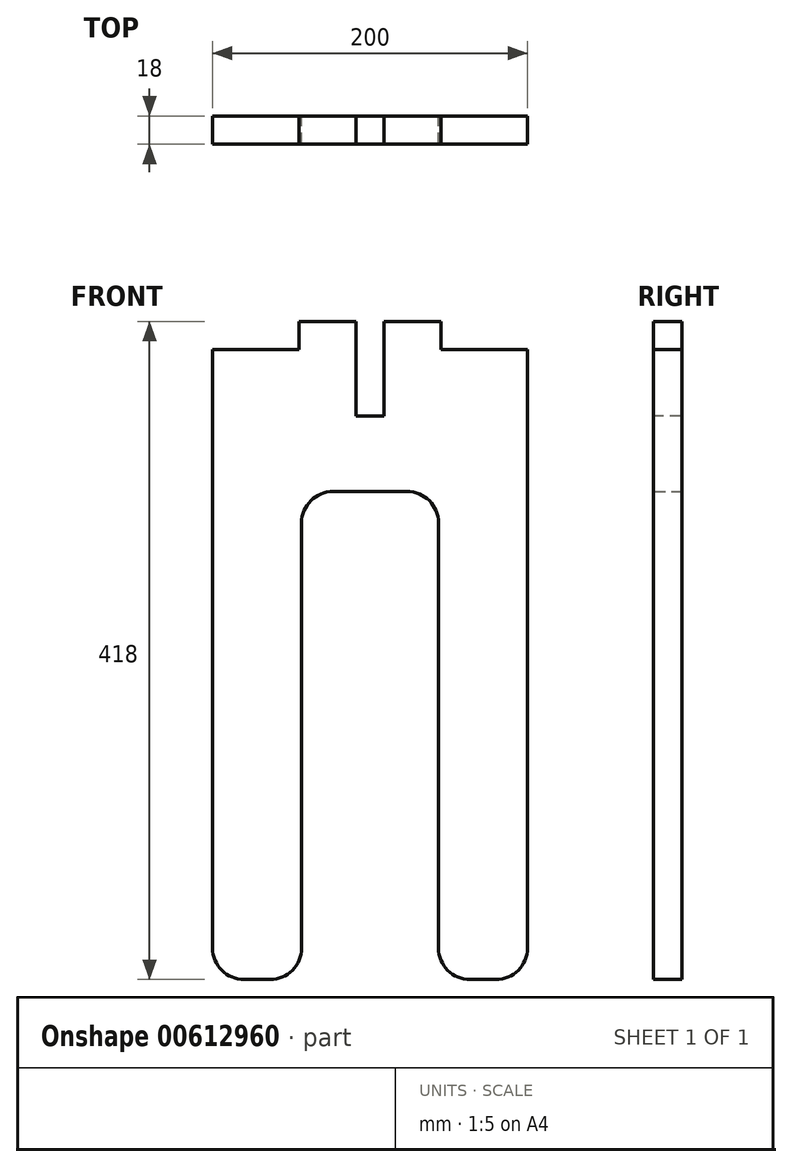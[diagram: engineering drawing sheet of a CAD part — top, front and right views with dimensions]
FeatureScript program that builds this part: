
annotation { "Feature Type Name" : "Feature", "Feature Type Description" : "" }
export const myFeature = defineFeature(function(context is Context, id is Id, definition is map)
    precondition{}
    {
        {
            var Q0;
            Q0=qCreatedBy(makeId("Front.planeOp"),FACE);
            var sketch = newSketch(context, id + "F0", { "sketchPlane" : qUnion([Q0])});
            skLineSegment(sketch, "E0.bottom", {"start": v(78.55, -167.28) * mm, "end": v(62.03, -167.28) * mm});
            skLineSegment(sketch, "E0.top", {"start": v(98.55, 232.72) * mm, "end": v(43.55, 232.72) * mm});
            skLineSegment(sketch, "E0.left", {"start": v(98.55, -147.28) * mm, "end": v(98.55, 232.72) * mm});
            skLineSegment(sketch, "E0.right", {"start": v(-101.45, -147.28) * mm, "end": v(-101.45, 232.72) * mm});
            skPoint(sketch, "E0.middle", {"position": v(-1.45, 32.72) * mm});
            skLineSegment(sketch, "E1.top", {"start": v(22.03, 142.72) * mm, "end": v(-24.93, 142.72) * mm});
            skLineSegment(sketch, "E1.left", {"start": v(42.03, -77.28) * mm, "end": v(42.03, 122.72) * mm});
            skLineSegment(sketch, "E1.right", {"start": v(-44.93, -77.28) * mm, "end": v(-44.93, 122.72) * mm});
            skLineSegment(sketch, "E2", {"start": v(-44.93, -77.28) * mm, "end": v(-44.93, -147.28) * mm});
            skLineSegment(sketch, "E3", {"start": v(42.03, -147.28) * mm, "end": v(42.03, -77.28) * mm});
            skLineSegment(sketch, "E4.trimOffspring", {"start": v(-64.93, -167.28) * mm, "end": v(-81.45, -167.28) * mm});
            skPoint(sketch, "E5.orphan", {"position": v(42.03, -259.35) * mm});
            skPoint(sketch, "E6.visualSharp", {"position": v(-44.93, -167.28) * mm});
            skArc(sketch, "E6.filletArc", {"start": v(-64.93, -167.28) * mm, "mid": v(-50.79, -161.42) * mm, "end": v(-44.93, -147.28) * mm});
            skPoint(sketch, "E7.visualSharp", {"position": v(42.03, -167.28) * mm});
            skArc(sketch, "E7.filletArc", {"start": v(42.03, -147.28) * mm, "mid": v(47.89, -161.42) * mm, "end": v(62.03, -167.28) * mm});
            skPoint(sketch, "E8.visualSharp", {"position": v(98.55, -167.28) * mm});
            skArc(sketch, "E8.filletArc", {"start": v(78.55, -167.28) * mm, "mid": v(92.7, -161.42) * mm, "end": v(98.55, -147.28) * mm});
            skPoint(sketch, "E9.visualSharp", {"position": v(-101.45, -167.28) * mm});
            skArc(sketch, "E9.filletArc", {"start": v(-101.45, -147.28) * mm, "mid": v(-95.6, -161.42) * mm, "end": v(-81.45, -167.28) * mm});
            skPoint(sketch, "E10.visualSharp", {"position": v(42.03, 142.72) * mm});
            skArc(sketch, "E10.filletArc", {"start": v(42.03, 122.72) * mm, "mid": v(36.17, 136.86) * mm, "end": v(22.03, 142.72) * mm});
            skPoint(sketch, "E11.visualSharp", {"position": v(-44.93, 142.72) * mm});
            skArc(sketch, "E11.filletArc", {"start": v(-24.93, 142.72) * mm, "mid": v(-39.07, 136.86) * mm, "end": v(-44.93, 122.72) * mm});
            skLineSegment(sketch, "E12.trimOffspring", {"start": v(43.55, 232.72) * mm, "end": v(43.55, 250.72) * mm});
            skLineSegment(sketch, "E13.trimOffspring", {"start": v(-46.45, 232.72) * mm, "end": v(-46.45, 250.72) * mm});
            skLineSegment(sketch, "E14.trimOffspring", {"start": v(-46.45, 232.72) * mm, "end": v(-101.45, 232.72) * mm});
            skLineSegment(sketch, "E15", {"start": v(-46.45, 250.72) * mm, "end": v(43.55, 250.72) * mm});
            skSolve(sketch);
        }
        {
            var Q0;
            Q0 = qSketchRegion(id + "F0", true);
            extrude(context, id + "F1", {"entities" : qUnion([Q0]), "depth" : 18 * mm, "offsetDistance" : 25 * mm});
        }
        {
            var Q0;
            Q0=makeQuery(id+"F1.opExtrude","CAP_FACE",FACE,{"disambiguationData":[OSD([sQuery(id+"F0.wireOp",EDGE,"E0.bottom"),sQuery(id+"F0.wireOp",EDGE,"E0.top"),sQuery(id+"F0.wireOp",EDGE,"E0.left"),sQuery(id+"F0.wireOp",EDGE,"E0.right"),sQuery(id+"F0.wireOp",EDGE,"E1.top"),sQuery(id+"F0.wireOp",EDGE,"E1.left"),sQuery(id+"F0.wireOp",EDGE,"E1.right"),sQuery(id+"F0.wireOp",EDGE,"E2"),sQuery(id+"F0.wireOp",EDGE,"E3"),sQuery(id+"F0.wireOp",EDGE,"E4.trimOffspring"),sQuery(id+"F0.wireOp",EDGE,"E6.filletArc"),sQuery(id+"F0.wireOp",EDGE,"E7.filletArc"),sQuery(id+"F0.wireOp",EDGE,"E8.filletArc"),sQuery(id+"F0.wireOp",EDGE,"E9.filletArc"),sQuery(id+"F0.wireOp",EDGE,"E10.filletArc"),sQuery(id+"F0.wireOp",EDGE,"E11.filletArc"),sQuery(id+"F0.wireOp",EDGE,"E12.trimOffspring"),sQuery(id+"F0.wireOp",EDGE,"E13.trimOffspring"),sQuery(id+"F0.wireOp",EDGE,"E14.trimOffspring"),sQuery(id+"F0.wireOp",EDGE,"E15")])],"isStart":false});
            var sketch = newSketch(context, id + "F2", { "sketchPlane" : qUnion([Q0])});
            skLineSegment(sketch, "E16.bottom", {"start": v(-10.45, 190.72) * mm, "end": v(7.55, 190.72) * mm});
            skLineSegment(sketch, "E16.top", {"start": v(-10.45, 310.72) * mm, "end": v(7.55, 310.72) * mm});
            skLineSegment(sketch, "E16.left", {"start": v(-10.45, 190.72) * mm, "end": v(-10.45, 310.72) * mm});
            skLineSegment(sketch, "E16.right", {"start": v(7.55, 190.72) * mm, "end": v(7.55, 310.72) * mm});
            skPoint(sketch, "E16.middle", {"position": v(-1.45, 250.72) * mm});
            skSolve(sketch);
        }
        {
            var Q0;
            Q0 = qSketchRegion(id + "F2", true);
            extrude(context, id + "F3", {"entities" : qUnion([Q0]), "operationType" : NewBodyOperationType.REMOVE, "oppositeDirection" : true, "depth" : 25 * mm, "offsetDistance" : 25 * mm});
        }
    });
